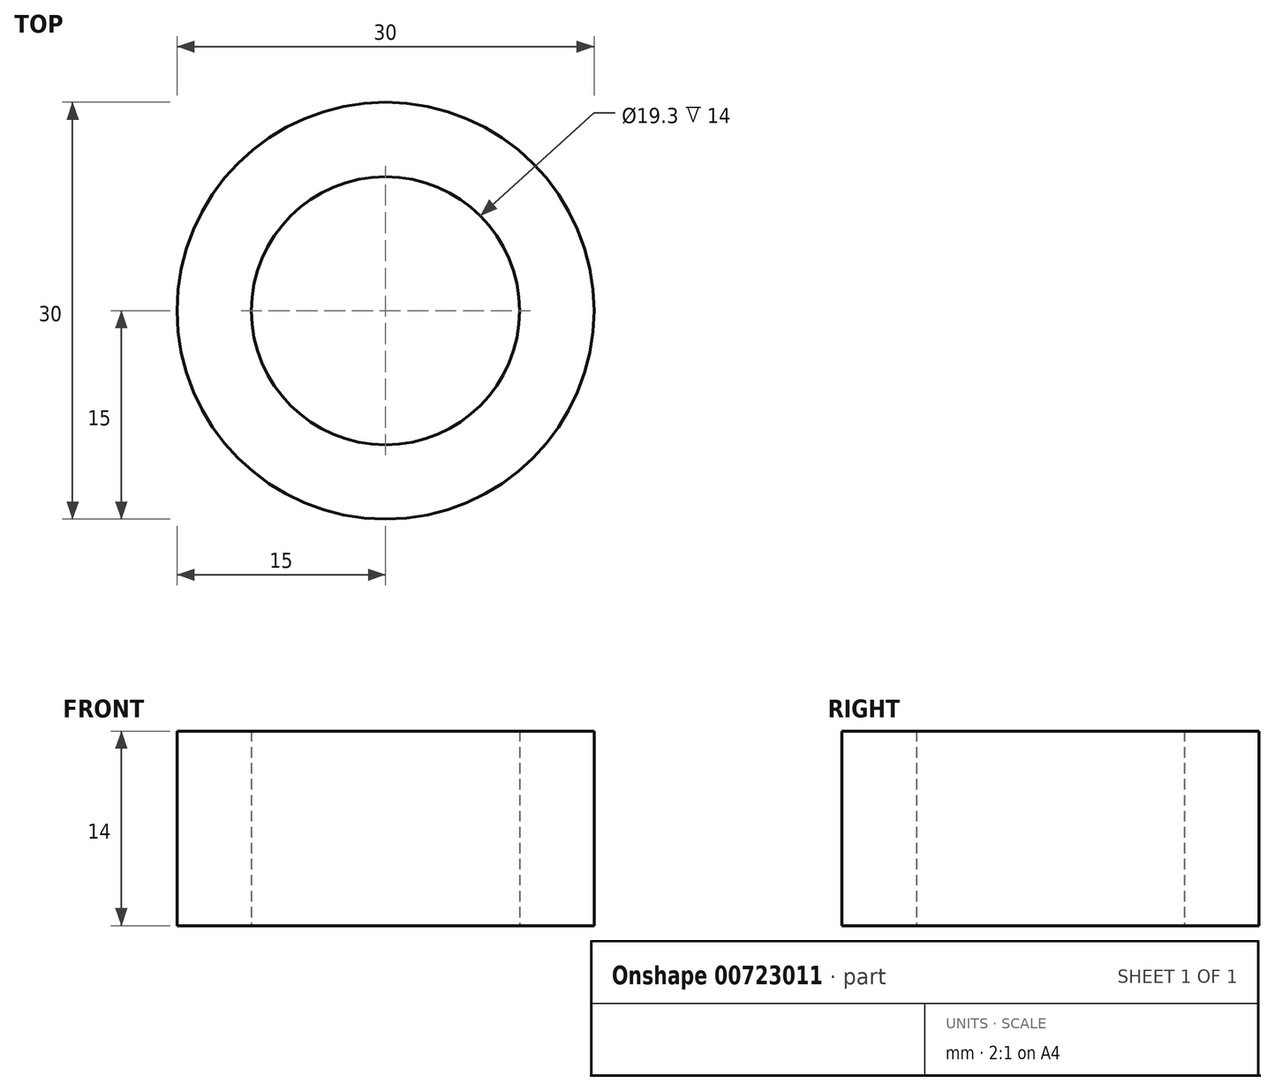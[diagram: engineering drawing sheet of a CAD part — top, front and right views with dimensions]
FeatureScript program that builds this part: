
annotation { "Feature Type Name" : "Feature", "Feature Type Description" : "" }
export const myFeature = defineFeature(function(context is Context, id is Id, definition is map)
    precondition{}
    {
        {
            var Q0;
            Q0=qCreatedBy(makeId("Top.planeOp"),FACE);
            var sketch = newSketch(context, id + "F0", { "sketchPlane" : qUnion([Q0])});
            skCircle(sketch, "E0", {"center": v(0, 0) * mm, "radius": 9.65 * mm});
            skCircle(sketch, "E1", {"center": v(0, 0) * mm, "radius": 15 * mm});
            skSolve(sketch);
        }
        {
            var Q0;
            Q0=makeQuery(id+"F0.imprint","IMPRINT",FACE,{"disambiguationData":[TD([[makeQuery(id+"F0.imprint","IMPRINT",EDGE,{"derivedFrom":sQuery(id+"F0.wireOp",EDGE,"E0")}),-1.0]])]});
            extrude(context, id + "F1", {"entities" : qUnion([Q0]), "depth" : 14 * mm, "offsetDistance" : 25 * mm});
        }
    });
